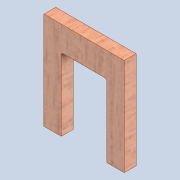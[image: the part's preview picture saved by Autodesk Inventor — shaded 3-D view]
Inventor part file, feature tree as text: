
AUTODESK INVENTOR PART (.ipt)
format: ipt  version: 2020 (Build 240168000, 168)  size: 163,840 bytes
history: native  units: mm
features: reference x4, other x3, extrude x2, sketch x2, fillet x1
ambient origin geometry x8: Origin, YZ Plane, XZ Plane, XY Plane, X Axis, Y Axis, Z Axis, Center Point
bodies: Solid1 (feature_tree)
feature tree (12):
  extrude  "Extrusion1"  Depth=66.0mm
  extrude  "Extrusion2"  TaperAngle=0.0deg  [1 undecoded]
  fillet  "Fillet1"  Radius=2.0mm
  sketch  "Sketch1"  dims[d0=54.5mm d1=66.0mm]
  sketch  "Sketch2"  dims[d2=8.0mm d3=0.0mm d6=0.0mm d7=0.0mm d29=2.0mm d30=2.0mm d32=2.0mm d33=1.5mm]
  reference  "Reference8"
  reference  "Reference9"
  reference  "Reference10"
  reference  "Reference11"
  parser-record x1  (decoder bookkeeping rows leaked as tree rows — omitted from the tree; the rows remain in map.json)
  other  "0005-00-00 Ansamblu_General.iam"
  other  "Inlet Module Plug Fuse Switch Male Power Socket 10A 250V 3 Pin IEC320 C14.ipt:82"
note: 1 required parameter value undecoded (feature->parameter linkage not recoverable at this tier; creation-order binding heuristic only, values carry confidence <= 0.55)
note: 1 file-system path scrubbed to <path> (originals preserved in map.json)
